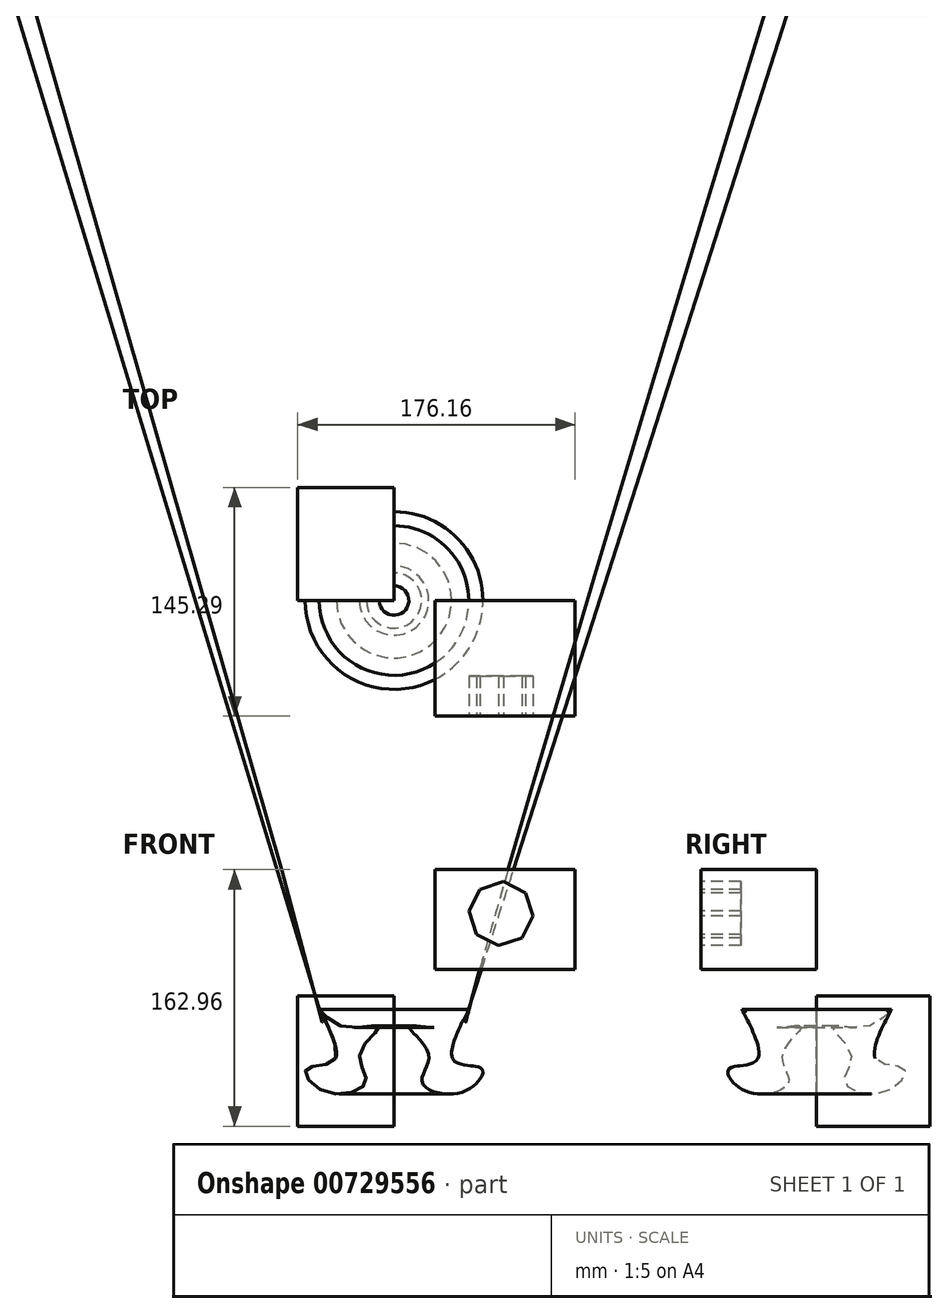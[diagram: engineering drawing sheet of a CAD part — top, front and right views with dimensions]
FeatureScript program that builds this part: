
annotation { "Feature Type Name" : "Feature", "Feature Type Description" : "" }
export const myFeature = defineFeature(function(context is Context, id is Id, definition is map)
    precondition{}
    {
        {
            var Q0;
            Q0=qCreatedBy(makeId("Front.planeOp"),FACE);
            var sketch = newSketch(context, id + "F0", { "sketchPlane" : qUnion([Q0])});
            skLineSegment(sketch, "E0", {"start": v(0, 63.5) * mm, "end": v(88.9, 63.5) * mm});
            skLineSegment(sketch, "E1", {"start": v(88.9, 63.5) * mm, "end": v(88.9, 0) * mm});
            skLineSegment(sketch, "E2", {"start": v(0, 63.5) * mm, "end": v(0, 0) * mm});
            skLineSegment(sketch, "E3", {"start": v(0, 0) * mm, "end": v(88.9, 0) * mm});
            skSolve(sketch);
        }
        {
            var Q0;
            Q0 = qSketchRegion(id + "F0", true);
            extrude(context, id + "F1", {"entities" : qUnion([Q0]), "depth" : 73.4 * mm, "offsetDistance" : 25.4 * mm});
        }
        {
            var Q0;
            Q0=makeQuery(id+"F1.opExtrude","SWEPT_FACE",FACE,{"disambiguationData":[OSD([sQuery(id+"F0.wireOp",EDGE,"E3")])]});
            var sketch = newSketch(context, id + "F2", { "sketchPlane" : qUnion([Q0])});
            skLineSegment(sketch, "E4", {"start": v(45.73, 26.46) * mm, "end": v(45.73, 62.63) * mm});
            skLineSegment(sketch, "E5", {"start": v(45.73, 62.63) * mm, "end": v(19.46, 62.63) * mm});
            skLineSegment(sketch, "E6", {"start": v(19.46, 62.63) * mm, "end": v(19.46, 26.46) * mm});
            skLineSegment(sketch, "E7", {"start": v(19.46, 26.46) * mm, "end": v(45.73, 26.46) * mm});
            skCircle(sketch, "E8", {"center": v(65.96, 37.36) * mm, "radius": 8.9 * mm});
            skSolve(sketch);
        }
        {
            var Q0;
            Q0=sQuery(id+"F2.wireOp",EDGE,"E8");
            extrude(context, id + "F3", {"bodyType" : ToolBodyType.SURFACE, "surfaceEntities" : qUnion([Q0]), "depth" : 35.05 * mm, "offsetDistance" : 25.4 * mm});
        }
        {
            var Q0;
            Q0=makeQuery(id+"F1.opExtrude","CAP_FACE",FACE,{"disambiguationData":[OSD([sQuery(id+"F0.wireOp",EDGE,"E0"),sQuery(id+"F0.wireOp",EDGE,"E1"),sQuery(id+"F0.wireOp",EDGE,"E2"),sQuery(id+"F0.wireOp",EDGE,"E3")])],"isStart":false});
            var sketch = newSketch(context, id + "F4", { "sketchPlane" : qUnion([Q0])});
            skCircle(sketch, "E9.cCircle", {"center": v(41.89, 35.51) * mm, "radius": 18.82 * mm, "construction": true});
            skLineSegment(sketch, "E9.0", {"start": v(43.5, 55.82) * mm, "end": v(57.39, 48.73) * mm});
            skLineSegment(sketch, "E9.1", {"start": v(57.39, 48.73) * mm, "end": v(62.2, 33.9) * mm});
            skLineSegment(sketch, "E9.2", {"start": v(62.2, 33.9) * mm, "end": v(55.1, 20.01) * mm});
            skLineSegment(sketch, "E9.3", {"start": v(55.1, 20.01) * mm, "end": v(40.28, 15.2) * mm});
            skLineSegment(sketch, "E9.4", {"start": v(40.28, 15.2) * mm, "end": v(26.39, 22.3) * mm});
            skLineSegment(sketch, "E9.5", {"start": v(26.39, 22.3) * mm, "end": v(21.58, 37.12) * mm});
            skLineSegment(sketch, "E9.6", {"start": v(21.58, 37.12) * mm, "end": v(28.67, 51) * mm});
            skLineSegment(sketch, "E9.7", {"start": v(28.67, 51) * mm, "end": v(43.5, 55.82) * mm});
            skPoint(sketch, "E9.0.midPoint", {"position": v(50.44, 52.27) * mm});
            skSolve(sketch);
        }
        {
            var Q0;
            Q0=makeQuery(id+"F4.imprint","IMPRINT",FACE,{"disambiguationData":[TD([[makeQuery(id+"F4.imprint","IMPRINT",EDGE,{"derivedFrom":sQuery(id+"F4.wireOp",EDGE,"E9.0")}),-1.0]])]});
            extrude(context, id + "F5", {"entities" : qUnion([Q0]), "operationType" : NewBodyOperationType.REMOVE, "oppositeDirection" : true, "depth" : 25.4 * mm, "offsetDistance" : 25.4 * mm});
        }
        {
            var Q0;
            Q0=qCreatedBy(makeId("Front.planeOp"),FACE);
            var sketch = newSketch(context, id + "F6", { "sketchPlane" : qUnion([Q0])});
            skLineSegment(sketch, "E10.bottom", {"start": v(-87.26, -16.78) * mm, "end": v(-26.06, -16.78) * mm});
            skLineSegment(sketch, "E10.top", {"start": v(-87.26, -99.46) * mm, "end": v(-26.06, -99.46) * mm});
            skLineSegment(sketch, "E10.left", {"start": v(-87.26, -16.78) * mm, "end": v(-87.26, -99.46) * mm});
            skLineSegment(sketch, "E10.right", {"start": v(-26.06, -16.78) * mm, "end": v(-26.06, -99.46) * mm});
            skSolve(sketch);
        }
        {
            var Q0;
            Q0 = qSketchRegion(id + "F6", true);
            extrude(context, id + "F7", {"entities" : qUnion([Q0]), "oppositeDirection" : true, "depth" : 71.88 * mm, "offsetDistance" : 25.4 * mm});
        }
        {
            var Q0;
            Q0=makeQuery(id+"F7.opExtrude","CAP_FACE",FACE,{"disambiguationData":[OSD([sQuery(id+"F6.wireOp",EDGE,"E10.bottom"),sQuery(id+"F6.wireOp",EDGE,"E10.top"),sQuery(id+"F6.wireOp",EDGE,"E10.left"),sQuery(id+"F6.wireOp",EDGE,"E10.right")])],"isStart":true});
            var sketch = newSketch(context, id + "F8", { "sketchPlane" : qUnion([Q0])});
            skFitSpline(sketch, "E11", {"points": [v(-63.27, -56.48) * mm, v(-73.51, -25.56) * mm, v(-60.05, -35.65) * mm, v(-35.46, -36.2) * mm, v(-47.94, -53.97) * mm, v(-43.84, -71.57) * mm, v(-69.69, -77.72) * mm, v(-81.74, -63.05) * mm, v(-63.27, -56.48) * mm]});
            skSolve(sketch);
        }
        {
            var Q0;
            Q0=makeQuery(id+"F8.imprint","IMPRINT",FACE,{"disambiguationData":[TD([[makeQuery(id+"F8.imprint","IMPRINT",EDGE,{"derivedFrom":sQuery(id+"F8.wireOp",EDGE,"E11")}),-1.0]])]});
            var Q1;
            Q1=makeQuery(id+"F7.opExtrude","CAP_EDGE",EDGE,{"disambiguationData":[OSD([sQuery(id+"F6.wireOp",EDGE,"E10.right")])],"isStart":true});
            revolve(context, id + "F9", {"operationType" : NewBodyOperationType.ADD, "surfaceOperationType" : NewSurfaceOperationType.NEW, "entities" : qUnion([Q0]), "axis" : qUnion([Q1]), "revolveType" : RevolveType.FULL, "oppositeDirection" : true});
        }
    });
